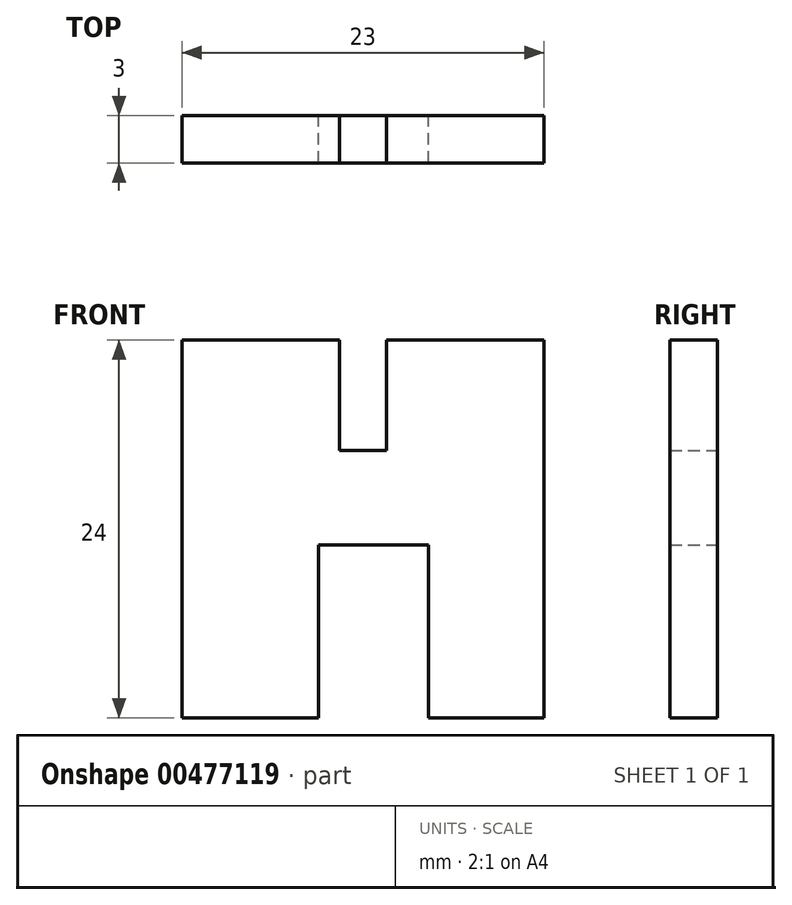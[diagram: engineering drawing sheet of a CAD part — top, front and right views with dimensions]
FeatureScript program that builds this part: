
annotation { "Feature Type Name" : "Feature", "Feature Type Description" : "" }
export const myFeature = defineFeature(function(context is Context, id is Id, definition is map)
    precondition{}
    {
        {
            var Q0;
            Q0=qCreatedBy(makeId("Front.planeOp"),FACE);
            var sketch = newSketch(context, id + "F0", { "sketchPlane" : qUnion([Q0])});
            skLineSegment(sketch, "E0", {"start": v(-60.6, 35.85) * mm, "end": v(-60.6, 11.85) * mm});
            skLineSegment(sketch, "E1", {"start": v(-60.6, 11.85) * mm, "end": v(-51.93, 11.85) * mm});
            skLineSegment(sketch, "E2", {"start": v(-51.93, 11.85) * mm, "end": v(-51.93, 22.85) * mm});
            skLineSegment(sketch, "E3", {"start": v(-51.93, 22.85) * mm, "end": v(-44.93, 22.85) * mm});
            skLineSegment(sketch, "E4", {"start": v(-44.93, 22.85) * mm, "end": v(-44.93, 11.85) * mm});
            skLineSegment(sketch, "E5", {"start": v(-44.93, 11.85) * mm, "end": v(-37.6, 11.85) * mm});
            skLineSegment(sketch, "E6", {"start": v(-37.6, 11.85) * mm, "end": v(-37.6, 35.85) * mm});
            skLineSegment(sketch, "E7", {"start": v(-37.6, 35.85) * mm, "end": v(-47.6, 35.85) * mm});
            skLineSegment(sketch, "E8", {"start": v(-47.6, 35.85) * mm, "end": v(-47.6, 28.85) * mm});
            skLineSegment(sketch, "E9", {"start": v(-47.6, 28.85) * mm, "end": v(-50.6, 28.85) * mm});
            skLineSegment(sketch, "E10", {"start": v(-50.6, 28.85) * mm, "end": v(-50.6, 35.85) * mm});
            skLineSegment(sketch, "E11", {"start": v(-50.6, 35.85) * mm, "end": v(-60.6, 35.85) * mm});
            skSolve(sketch);
        }
        {
            var Q0;
            Q0 = qSketchRegion(id + "F0", true);
            extrude(context, id + "F1", {"entities" : qUnion([Q0]), "depth" : 3 * mm});
        }
    });
